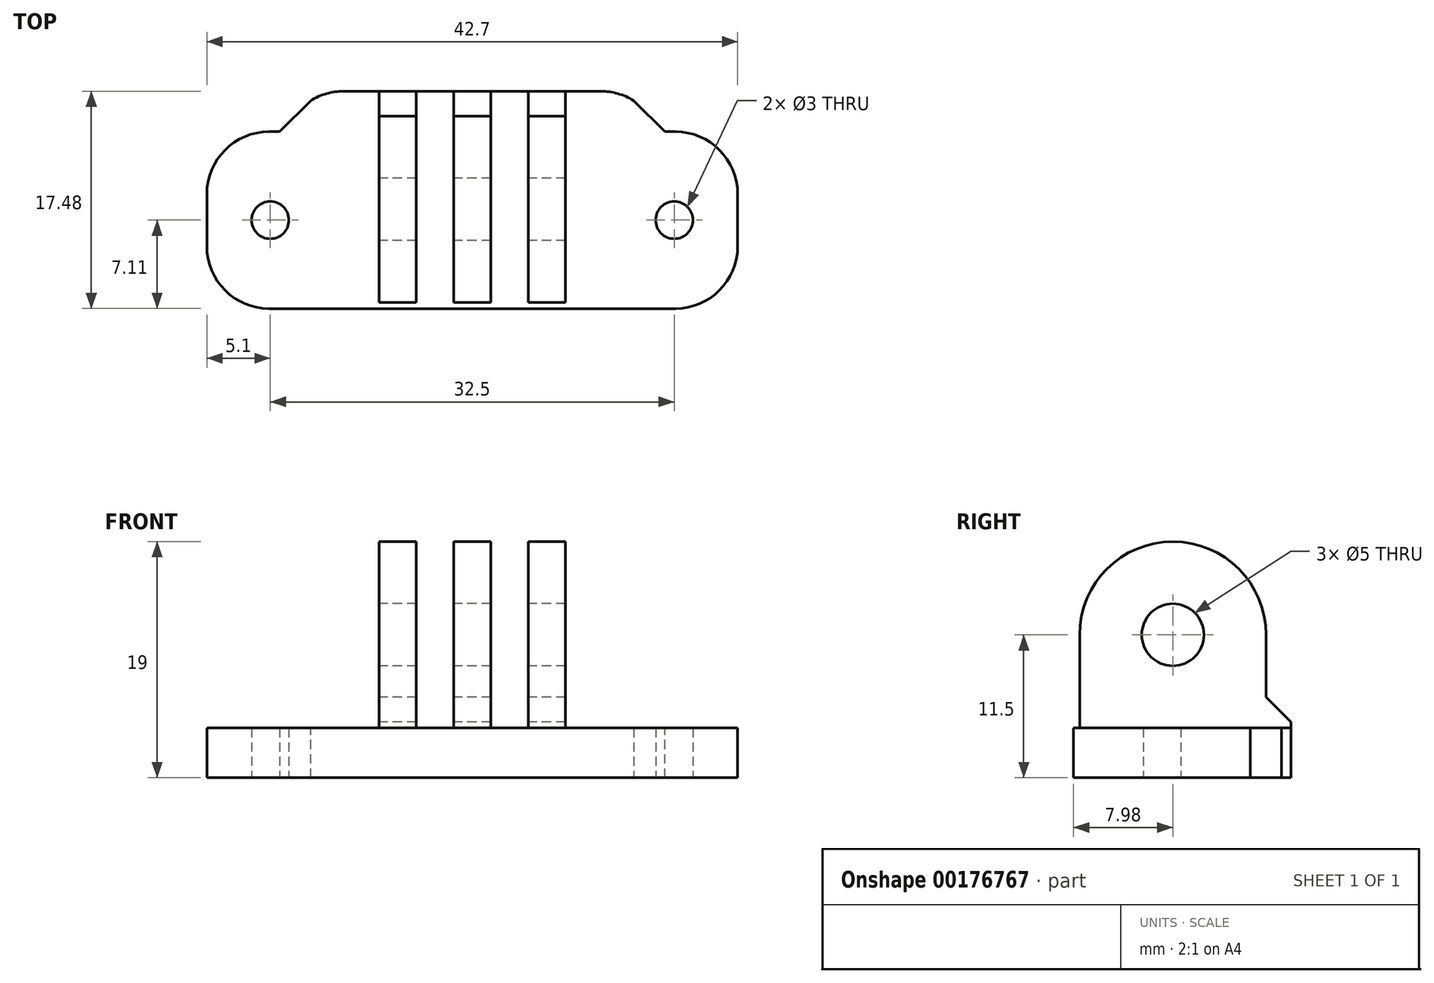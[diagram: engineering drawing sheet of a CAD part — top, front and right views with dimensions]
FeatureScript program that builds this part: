
annotation { "Feature Type Name" : "Feature", "Feature Type Description" : "" }
export const myFeature = defineFeature(function(context is Context, id is Id, definition is map)
    precondition{}
    {
        {
            var Q0;
            Q0=qCreatedBy(makeId("Top.planeOp"),FACE);
            var sketch = newSketch(context, id + "F0", { "sketchPlane" : qUnion([Q0])});
            skLineSegment(sketch, "E0.bottom", {"start": v(-21.35, 7.11) * mm, "end": v(21.35, 7.11) * mm});
            skLineSegment(sketch, "E0.top", {"start": v(-21.35, -7.11) * mm, "end": v(21.35, -7.11) * mm});
            skLineSegment(sketch, "E0.left", {"start": v(-21.35, 7.11) * mm, "end": v(-21.35, -7.11) * mm});
            skLineSegment(sketch, "E0.right", {"start": v(21.35, 7.11) * mm, "end": v(21.35, -7.11) * mm});
            skPoint(sketch, "E0.middle", {"position": v(0, 0) * mm});
            skCircle(sketch, "E1", {"center": v(-16.25, 0) * mm, "radius": 1.5 * mm});
            skCircle(sketch, "E2.MirrorC", {"center": v(16.25, 0) * mm, "radius": 1.5 * mm});
            skLineSegment(sketch, "E3", {"start": v(-13, 7.11) * mm, "end": v(-13, 10.37) * mm});
            skLineSegment(sketch, "E4", {"start": v(-13, 10.37) * mm, "end": v(13, 10.37) * mm});
            skLineSegment(sketch, "E5", {"start": v(13, 10.37) * mm, "end": v(13, 7.11) * mm});
            skLineSegment(sketch, "E6", {"start": v(13, 7.11) * mm, "end": v(0, 7.11) * mm});
            skLineSegment(sketch, "E7", {"start": v(0, 7.11) * mm, "end": v(-13, 7.11) * mm});
            skLineSegment(sketch, "E8.bottom", {"start": v(-7.5, 8.37) * mm, "end": v(-4.5, 8.37) * mm});
            skLineSegment(sketch, "E8.top", {"start": v(-7.5, -6.63) * mm, "end": v(-4.5, -6.63) * mm});
            skLineSegment(sketch, "E8.left", {"start": v(-7.5, 8.37) * mm, "end": v(-7.5, -6.63) * mm});
            skLineSegment(sketch, "E8.right", {"start": v(-4.5, 8.37) * mm, "end": v(-4.5, -6.63) * mm});
            skPoint(sketch, "E8.middle", {"position": v(-6, 0.87) * mm});
            skLineSegment(sketch, "E9.bottom", {"start": v(-1.5, 8.37) * mm, "end": v(1.5, 8.37) * mm});
            skLineSegment(sketch, "E9.top", {"start": v(-1.5, -6.63) * mm, "end": v(1.5, -6.63) * mm});
            skLineSegment(sketch, "E9.left", {"start": v(-1.5, 8.37) * mm, "end": v(-1.5, -6.63) * mm});
            skLineSegment(sketch, "E9.right", {"start": v(1.5, 8.37) * mm, "end": v(1.5, -6.63) * mm});
            skLineSegment(sketch, "E10.bottom", {"start": v(4.5, 8.37) * mm, "end": v(7.5, 8.37) * mm});
            skLineSegment(sketch, "E10.top", {"start": v(4.5, -6.63) * mm, "end": v(7.5, -6.63) * mm});
            skLineSegment(sketch, "E10.left", {"start": v(4.5, 8.37) * mm, "end": v(4.5, -6.63) * mm});
            skLineSegment(sketch, "E10.right", {"start": v(7.5, 8.37) * mm, "end": v(7.5, -6.63) * mm});
            skPoint(sketch, "E10.middle", {"position": v(6, 0.87) * mm});
            skLineSegment(sketch, "E11", {"start": v(-4.5, 8.37) * mm, "end": v(-1.5, 8.37) * mm});
            skLineSegment(sketch, "E12", {"start": v(4.5, 8.37) * mm, "end": v(1.5, 8.37) * mm});
            skLineSegment(sketch, "E13", {"start": v(-1.5, 0.87) * mm, "end": v(1.5, 0.87) * mm, "construction": true});
            skPoint(sketch, "E14", {"position": v(0, 0.87) * mm});
            skSolve(sketch);
        }
        {
            var Q0;
            Q0 = qSketchRegion(id + "F0", true);
            var Q1;
            {var subQ5=sQuery(id+"F0.wireOp",EDGE,"E8.top");Q1=makeQuery(id+"F0.imprint","IMPRINT",FACE,{"disambiguationData":[TD([[makeQuery(id+"F0.imprint","IMPRINT",EDGE,{"derivedFrom":subQ5}),1.0]])]});}
            var Q2;
            {var subQ5=sQuery(id+"F0.wireOp",EDGE,"E8.bottom");Q2=makeQuery(id+"F0.imprint","IMPRINT",FACE,{"disambiguationData":[TD([[makeQuery(id+"F0.imprint","IMPRINT",EDGE,{"derivedFrom":subQ5}),-1.0]])]});}
            var Q3;
            {var subQ5=sQuery(id+"F0.wireOp",EDGE,"E11");Q3=makeQuery(id+"F0.imprint","IMPRINT",FACE,{"disambiguationData":[TD([[makeQuery(id+"F0.imprint","IMPRINT",EDGE,{"derivedFrom":subQ5}),-1.0]])]});}
            var Q4;
            {var subQ1=sQuery(id+"F0.wireOp",EDGE,"E9.bottom");Q4=makeQuery(id+"F0.imprint","IMPRINT",FACE,{"disambiguationData":[TD([[makeQuery(id+"F0.imprint","IMPRINT",EDGE,{"derivedFrom":subQ1}),-1.0]])]});}
            var Q5;
            {var subQ0=sQuery(id+"F0.wireOp",EDGE,"E9.top");Q5=makeQuery(id+"F0.imprint","IMPRINT",FACE,{"disambiguationData":[TD([[makeQuery(id+"F0.imprint","IMPRINT",EDGE,{"derivedFrom":subQ0}),1.0]])]});}
            var Q6;
            {var subQ5=sQuery(id+"F0.wireOp",EDGE,"E12");Q6=makeQuery(id+"F0.imprint","IMPRINT",FACE,{"disambiguationData":[TD([[makeQuery(id+"F0.imprint","IMPRINT",EDGE,{"derivedFrom":subQ5}),1.0]])]});}
            var Q7;
            {var subQ5=sQuery(id+"F0.wireOp",EDGE,"E10.top");Q7=makeQuery(id+"F0.imprint","IMPRINT",FACE,{"disambiguationData":[TD([[makeQuery(id+"F0.imprint","IMPRINT",EDGE,{"derivedFrom":subQ5}),1.0]])]});}
            var Q8;
            {var subQ5=sQuery(id+"F0.wireOp",EDGE,"E10.bottom");Q8=makeQuery(id+"F0.imprint","IMPRINT",FACE,{"disambiguationData":[TD([[makeQuery(id+"F0.imprint","IMPRINT",EDGE,{"derivedFrom":subQ5}),-1.0]])]});}
            extrude(context, id + "F1", {"entities" : qUnion([Q0, Q1, Q2, Q3, Q4, Q5, Q6, Q7, Q8]), "depth" : 4 * mm});
        }
        {
            var Q0;
            {var subQ5=sQuery(id+"F0.wireOp",EDGE,"E8.top");Q0=makeQuery(id+"F0.imprint","IMPRINT",FACE,{"disambiguationData":[TD([[makeQuery(id+"F0.imprint","IMPRINT",EDGE,{"derivedFrom":subQ5}),1.0]])]});}
            var Q1;
            {var subQ5=sQuery(id+"F0.wireOp",EDGE,"E8.bottom");Q1=makeQuery(id+"F0.imprint","IMPRINT",FACE,{"disambiguationData":[TD([[makeQuery(id+"F0.imprint","IMPRINT",EDGE,{"derivedFrom":subQ5}),-1.0]])]});}
            var Q2;
            {var subQ1=sQuery(id+"F0.wireOp",EDGE,"E9.bottom");Q2=makeQuery(id+"F0.imprint","IMPRINT",FACE,{"disambiguationData":[TD([[makeQuery(id+"F0.imprint","IMPRINT",EDGE,{"derivedFrom":subQ1}),-1.0]])]});}
            var Q3;
            {var subQ0=sQuery(id+"F0.wireOp",EDGE,"E9.top");Q3=makeQuery(id+"F0.imprint","IMPRINT",FACE,{"disambiguationData":[TD([[makeQuery(id+"F0.imprint","IMPRINT",EDGE,{"derivedFrom":subQ0}),1.0]])]});}
            var Q4;
            {var subQ5=sQuery(id+"F0.wireOp",EDGE,"E10.top");Q4=makeQuery(id+"F0.imprint","IMPRINT",FACE,{"disambiguationData":[TD([[makeQuery(id+"F0.imprint","IMPRINT",EDGE,{"derivedFrom":subQ5}),1.0]])]});}
            var Q5;
            {var subQ5=sQuery(id+"F0.wireOp",EDGE,"E10.bottom");Q5=makeQuery(id+"F0.imprint","IMPRINT",FACE,{"disambiguationData":[TD([[makeQuery(id+"F0.imprint","IMPRINT",EDGE,{"derivedFrom":subQ5}),-1.0]])]});}
            extrude(context, id + "F2", {"entities" : qUnion([Q0, Q1, Q2, Q3, Q4, Q5]), "operationType" : NewBodyOperationType.ADD, "depth" : (15 + 4) * mm});
        }
        {
            var Q0;
            Q0=makeQuery(id+"F2.opExtrude","CAP_EDGE",EDGE,{"disambiguationData":[OSD([sQuery(id+"F0.wireOp",EDGE,"E8.top")])],"isStart":false});
            var Q1;
            Q1=makeQuery(id+"F2.opExtrude","CAP_EDGE",EDGE,{"disambiguationData":[OSD([sQuery(id+"F0.wireOp",EDGE,"E9.top")])],"isStart":false});
            var Q2;
            Q2=makeQuery(id+"F2.opExtrude","CAP_EDGE",EDGE,{"disambiguationData":[OSD([sQuery(id+"F0.wireOp",EDGE,"E10.top")])],"isStart":false});
            var Q3;
            Q3=makeQuery(id+"F2.opExtrude","CAP_EDGE",EDGE,{"disambiguationData":[OSD([sQuery(id+"F0.wireOp",EDGE,"E10.bottom")])],"isStart":false});
            var Q4;
            Q4=makeQuery(id+"F2.opExtrude","CAP_EDGE",EDGE,{"disambiguationData":[OSD([sQuery(id+"F0.wireOp",EDGE,"E9.bottom")])],"isStart":false});
            var Q5;
            Q5=makeQuery(id+"F2.opExtrude","CAP_EDGE",EDGE,{"disambiguationData":[OSD([sQuery(id+"F0.wireOp",EDGE,"E8.bottom")])],"isStart":false});
            fillet(context, id + "F3", {"entities" : qUnion([Q0, Q1, Q2, Q3, Q4, Q5]), "radius" : (15 / 2) * mm, "tangentPropagation" : true, "allowEdgeOverflow" : false});
        }
        {
            var Q0;
            Q0=makeQuery(id+"F2.opExtrude","SWEPT_FACE",FACE,{"disambiguationData":[OSD([sQuery(id+"F0.wireOp",EDGE,"E8.left")])]});
            var sketch = newSketch(context, id + "F4", { "sketchPlane" : qUnion([Q0])});
            skCircle(sketch, "E15", {"center": v(-0.87, 11.5) * mm, "radius": 2.5 * mm});
            skSolve(sketch);
        }
        {
            var Q0;
            Q0 = qSketchRegion(id + "F4", true);
            extrude(context, id + "F5", {"entities" : qUnion([Q0]), "operationType" : NewBodyOperationType.REMOVE, "endBound" : BoundingType.THROUGH_ALL, "oppositeDirection" : true, "depth" : 25 * mm});
        }
        {
            var Q0;
            Q0=makeQuery(id+"F1.opExtrude","CAP_EDGE",EDGE,{"disambiguationData":[OSD([sQuery(id+"F0.wireOp",EDGE,"E8.left")])],"isStart":false});
            var Q1;
            Q1=makeQuery(id+"F1.opExtrude","CAP_EDGE",EDGE,{"disambiguationData":[OSD([sQuery(id+"F0.wireOp",EDGE,"E10.right")])],"isStart":false});
            var Q2;
            Q2=makeQuery(id+"F1.opExtrude","CAP_EDGE",EDGE,{"disambiguationData":[OSD([sQuery(id+"F0.wireOp",EDGE,"E10.top")])],"isStart":false});
            var Q3;
            Q3=makeQuery(id+"F1.opExtrude","CAP_EDGE",EDGE,{"disambiguationData":[OSD([sQuery(id+"F0.wireOp",EDGE,"E9.top")])],"isStart":false});
            var Q4;
            Q4=makeQuery(id+"F1.opExtrude","CAP_EDGE",EDGE,{"disambiguationData":[OSD([sQuery(id+"F0.wireOp",EDGE,"E8.top")])],"isStart":false});
            var Q5;
            Q5=makeQuery(id+"F1.opExtrude","CAP_EDGE",EDGE,{"disambiguationData":[OSD([sQuery(id+"F0.wireOp",EDGE,"E8.bottom")])],"isStart":false});
            var Q6;
            Q6=makeQuery(id+"F1.opExtrude","CAP_EDGE",EDGE,{"disambiguationData":[OSD([sQuery(id+"F0.wireOp",EDGE,"E9.bottom")])],"isStart":false});
            var Q7;
            Q7=makeQuery(id+"F1.opExtrude","CAP_EDGE",EDGE,{"disambiguationData":[OSD([sQuery(id+"F0.wireOp",EDGE,"E10.bottom")])],"isStart":false});
            var Q8;
            Q8=makeQuery(id+"F1.opExtrude","SWEPT_EDGE",EDGE,{"disambiguationData":[OSD([sQuery(id+"F0.wireOp",EDGE,"E0.bottom"),sQuery(id+"F0.wireOp",EDGE,"E5"),sQuery(id+"F0.wireOp",EDGE,"E6")])]});
            var Q9;
            Q9=makeQuery(id+"F1.opExtrude","SWEPT_EDGE",EDGE,{"disambiguationData":[OSD([sQuery(id+"F0.wireOp",EDGE,"E0.bottom"),sQuery(id+"F0.wireOp",EDGE,"E3"),sQuery(id+"F0.wireOp",EDGE,"E7")])]});
            var Q10;
            Q10=makeQuery(id+"F2.boolean.opBoolean","INTERSECT",EDGE,{"derivedFrom":[makeQuery(id+"F1.opExtrude","CAP_FACE",FACE,{"disambiguationData":[OSD([sQuery(id+"F0.wireOp",EDGE,"E0.bottom"),sQuery(id+"F0.wireOp",EDGE,"E0.top"),sQuery(id+"F0.wireOp",EDGE,"E0.left"),sQuery(id+"F0.wireOp",EDGE,"E0.right"),sQuery(id+"F0.wireOp",EDGE,"E1"),sQuery(id+"F0.wireOp",EDGE,"E2.MirrorC"),sQuery(id+"F0.wireOp",EDGE,"E3"),sQuery(id+"F0.wireOp",EDGE,"E4"),sQuery(id+"F0.wireOp",EDGE,"E5")])],"isStart":false}),makeQuery(id+"F2.opExtrude","SWEPT_FACE",FACE,{"disambiguationData":[OSD([sQuery(id+"F0.wireOp",EDGE,"E8.bottom")])]})]});
            var Q11;
            Q11=makeQuery(id+"F2.boolean.opBoolean","INTERSECT",EDGE,{"derivedFrom":[makeQuery(id+"F1.opExtrude","CAP_FACE",FACE,{"disambiguationData":[OSD([sQuery(id+"F0.wireOp",EDGE,"E0.bottom"),sQuery(id+"F0.wireOp",EDGE,"E0.top"),sQuery(id+"F0.wireOp",EDGE,"E0.left"),sQuery(id+"F0.wireOp",EDGE,"E0.right"),sQuery(id+"F0.wireOp",EDGE,"E1"),sQuery(id+"F0.wireOp",EDGE,"E2.MirrorC"),sQuery(id+"F0.wireOp",EDGE,"E3"),sQuery(id+"F0.wireOp",EDGE,"E4"),sQuery(id+"F0.wireOp",EDGE,"E5")])],"isStart":false}),makeQuery(id+"F2.opExtrude","SWEPT_FACE",FACE,{"disambiguationData":[OSD([sQuery(id+"F0.wireOp",EDGE,"E9.bottom")])]})]});
            var Q12;
            Q12=makeQuery(id+"F2.boolean.opBoolean","INTERSECT",EDGE,{"derivedFrom":[makeQuery(id+"F1.opExtrude","CAP_FACE",FACE,{"disambiguationData":[OSD([sQuery(id+"F0.wireOp",EDGE,"E0.bottom"),sQuery(id+"F0.wireOp",EDGE,"E0.top"),sQuery(id+"F0.wireOp",EDGE,"E0.left"),sQuery(id+"F0.wireOp",EDGE,"E0.right"),sQuery(id+"F0.wireOp",EDGE,"E1"),sQuery(id+"F0.wireOp",EDGE,"E2.MirrorC"),sQuery(id+"F0.wireOp",EDGE,"E3"),sQuery(id+"F0.wireOp",EDGE,"E4"),sQuery(id+"F0.wireOp",EDGE,"E5")])],"isStart":false}),makeQuery(id+"F2.opExtrude","SWEPT_FACE",FACE,{"disambiguationData":[OSD([sQuery(id+"F0.wireOp",EDGE,"E10.bottom")])]})]});
            chamfer(context, id + "F6", {"entities" : qUnion([Q0, Q1, Q2, Q3, Q4, Q5, Q6, Q7, Q8, Q9, Q10, Q11, Q12]), "width" : 2.5 * mm, "tangentPropagation" : true});
        }
        {
            var Q0;
            Q0=makeQuery(id+"F1.opExtrude","SWEPT_EDGE",EDGE,{"disambiguationData":[OSD([sQuery(id+"F0.wireOp",EDGE,"E4"),sQuery(id+"F0.wireOp",EDGE,"E5")])]});
            var Q1;
            Q1=makeQuery(id+"F1.opExtrude","SWEPT_EDGE",EDGE,{"disambiguationData":[OSD([sQuery(id+"F0.wireOp",EDGE,"E3"),sQuery(id+"F0.wireOp",EDGE,"E4")])]});
            var Q2;
            Q2=makeQuery(id+"F1.opExtrude","SWEPT_EDGE",EDGE,{"disambiguationData":[OSD([sQuery(id+"F0.wireOp",EDGE,"E0.bottom"),sQuery(id+"F0.wireOp",EDGE,"E0.left")])]});
            var Q3;
            Q3=makeQuery(id+"F1.opExtrude","SWEPT_EDGE",EDGE,{"disambiguationData":[OSD([sQuery(id+"F0.wireOp",EDGE,"E0.top"),sQuery(id+"F0.wireOp",EDGE,"E0.left")])]});
            var Q4;
            Q4=makeQuery(id+"F1.opExtrude","SWEPT_EDGE",EDGE,{"disambiguationData":[OSD([sQuery(id+"F0.wireOp",EDGE,"E0.top"),sQuery(id+"F0.wireOp",EDGE,"E0.right")])]});
            var Q5;
            Q5=makeQuery(id+"F1.opExtrude","SWEPT_EDGE",EDGE,{"disambiguationData":[OSD([sQuery(id+"F0.wireOp",EDGE,"E0.bottom"),sQuery(id+"F0.wireOp",EDGE,"E0.right")])]});
            fillet(context, id + "F7", {"entities" : qUnion([Q0, Q1, Q2, Q3, Q4, Q5]), "radius" : 5 * mm, "tangentPropagation" : true, "allowEdgeOverflow" : false});
        }
    });
